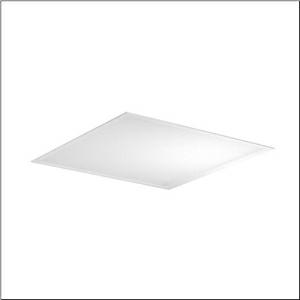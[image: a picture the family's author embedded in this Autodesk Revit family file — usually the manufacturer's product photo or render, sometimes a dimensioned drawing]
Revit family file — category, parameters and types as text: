
# Revit family: apollon_r__31_square_51mp12n72442_260a
name_source: partatom
category: Lighting Fixtures
units: mm (PartAtom-declared; Revit-internal decimal feet)

## family parameters
Cut with Voids When Loaded = No
Host = Face
Light Source = No
Part Type = Normal
Room Calculation Point = No
Round Connector Dimension = Use Diameter
Shared = No

## types (1)
- Apollon® 31 square (1 x LED, 4000 lm, 27.5 W, 4000K)
    Apparent Load = 28 VA
    CIE Flux Codes = 46 78 95 100 100
    Color Rendering = 80
    Color Temperature = 4000K
    Default Elevation = 1800 mm
    Description = Apollon® 31 square, office luminaire, primary optical cover: micro prismatic cover, of PMMA, CAT 2 (L<= 3000cd/m²), light emission: direct distribution, primary light characteristic: symmetric, installation type: lay-in mounting, LED, rated luminous flux: 4.000lm, luminous efficacy: 145lm/W, light colour: 840, colour temperature: 4000K, control gear: ON/OFF, with terminal, 3-pole, mains connection: 220..240V, AC, 50/60Hz, rated input power: 28W, housing, of aluminium, traffic white (RAL 9016), module: M600, length: 595mm, width: 595mm, height: 62mm, recess depth: 180mm, housing upper side, of sheet steel, coated, protection rating (complete): IP20, protection rating (on room side): IP40, insulation class (complete): insulation class II (safety insulation), certification: CE, ENEC, impact resistance: IK03, permissible operating ambient temperature: -20..+40°C, permissible storage temperature: -20..+60°C, packaging unit: 1 piece
    Height = 0 mm  [stored 0 ft]
    Lamp = 1 x LED
    Lamp Light Flux = 4000 lm
    Lamp Power = 27.5 W
    Lamp count = 1
    Length = 595 mm
    Luminous efficacy = 145 lm/W
    Manufacturer = Siteco
    ModVariant = No
    Model = 51MP12N72442
    Mounting Place = Ceiling
    Mounting Type = Recessed
    Number of Poles = 1
    OnlyDefault = Yes
    Power Factor = 1
    Product Name = Apollon® 31 square
    Product group = office luminaire | ceiling recessed
    ProductGroupID = 401
    Protection Class = Protection class II
    Protection Degree = IP 20
    RLX_Detail_Level = 1
    RLX_Emergency_Light_Flux = 0 lm
    RLX_Emergency_Type = 0
    RLX_Emergency_Type_DB = No
    RlxData = <blob elided: 12369 chars, md5=616f73cc>
    Socket = socket
    Standby Power = 0 W
    System Light Flux = 4000 lm
    System Power = 28 W
    Type Comments = Product without accessories
    Type Image = l_1291035.jpg
    URL = http://relux.com
    VarID = ---
    Voltage = 0 V
    Weight = 0.00 kg
    Width = 595 mm

note: [stored X ft] marks values corroborated as IEEE doubles in the binary element streams (Revit-internal decimal feet)

## geometry (parser evidence)
native form markers: Sweep x9
no freeform markers — native parametric forms only
